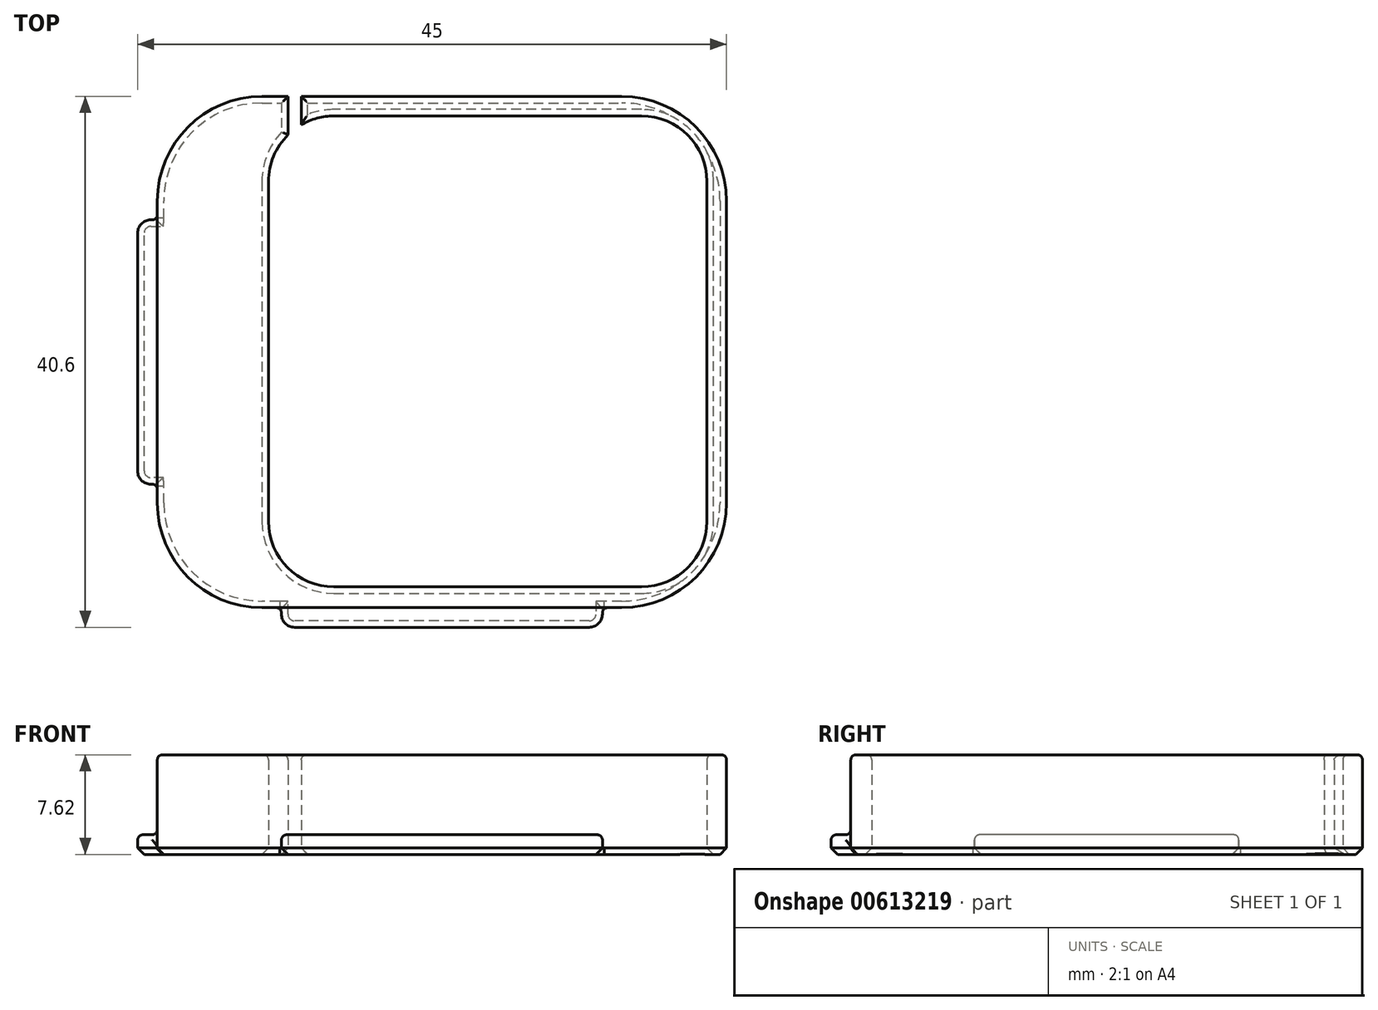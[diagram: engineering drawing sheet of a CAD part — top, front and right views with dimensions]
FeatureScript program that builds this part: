
annotation { "Feature Type Name" : "Feature", "Feature Type Description" : "" }
export const myFeature = defineFeature(function(context is Context, id is Id, definition is map)
    precondition{}
    {
        {
            var Q0;
            Q0=qCreatedBy(makeId("Top.planeOp"),FACE);
            var sketch = newSketch(context, id + "F0", { "sketchPlane" : qUnion([Q0])});
            skLineSegment(sketch, "E0.bottom", {"start": v(-14.69, 21.76) * mm, "end": v(-13.19, 21.76) * mm});
            skLineSegment(sketch, "E0.top", {"start": v(-14.69, -17.34) * mm, "end": v(12.81, -17.34) * mm});
            skLineSegment(sketch, "E0.left", {"start": v(-22.69, 13.76) * mm, "end": v(-22.69, -9.34) * mm});
            skLineSegment(sketch, "E0.right", {"start": v(20.81, 13.76) * mm, "end": v(20.81, -9.34) * mm});
            skLineSegment(sketch, "E1.bottom", {"start": v(14.31, 20.26) * mm, "end": v(-9.19, 20.26) * mm});
            skLineSegment(sketch, "E1.top", {"start": v(14.31, -15.74) * mm, "end": v(-9.19, -15.74) * mm});
            skLineSegment(sketch, "E1.left", {"start": v(19.31, 15.26) * mm, "end": v(19.31, -10.74) * mm});
            skLineSegment(sketch, "E1.right", {"start": v(-14.19, 15.26) * mm, "end": v(-14.19, -10.74) * mm});
            skPoint(sketch, "E2.visualSharp", {"position": v(-14.19, 20.26) * mm});
            skArc(sketch, "E2.filletArc", {"start": v(-9.19, 20.26) * mm, "mid": v(-10.48, 20.09) * mm, "end": v(-11.69, 19.59) * mm});
            skPoint(sketch, "E3.visualSharp", {"position": v(-14.19, -15.74) * mm});
            skArc(sketch, "E3.filletArc", {"start": v(-14.19, -10.74) * mm, "mid": v(-12.72, -14.28) * mm, "end": v(-9.19, -15.74) * mm});
            skPoint(sketch, "E4.visualSharp", {"position": v(19.31, -15.74) * mm});
            skArc(sketch, "E4.filletArc", {"start": v(14.31, -15.74) * mm, "mid": v(17.85, -14.28) * mm, "end": v(19.31, -10.74) * mm});
            skPoint(sketch, "E5.visualSharp", {"position": v(19.31, 20.26) * mm});
            skArc(sketch, "E5.filletArc", {"start": v(19.31, 15.26) * mm, "mid": v(17.85, 18.8) * mm, "end": v(14.31, 20.26) * mm});
            skPoint(sketch, "E6.visualSharp", {"position": v(-22.69, -17.34) * mm});
            skArc(sketch, "E6.filletArc", {"start": v(-22.69, -9.34) * mm, "mid": v(-20.35, -15) * mm, "end": v(-14.69, -17.34) * mm});
            skPoint(sketch, "E7.visualSharp", {"position": v(-22.69, 21.76) * mm});
            skArc(sketch, "E7.filletArc", {"start": v(-14.69, 21.76) * mm, "mid": v(-20.35, 19.41) * mm, "end": v(-22.69, 13.76) * mm});
            skPoint(sketch, "E8.visualSharp", {"position": v(20.81, 21.76) * mm});
            skArc(sketch, "E8.filletArc", {"start": v(20.81, 13.76) * mm, "mid": v(18.47, 19.41) * mm, "end": v(12.81, 21.76) * mm});
            skPoint(sketch, "E9.visualSharp", {"position": v(20.81, -17.34) * mm});
            skArc(sketch, "E9.filletArc", {"start": v(12.81, -17.34) * mm, "mid": v(18.47, -15) * mm, "end": v(20.81, -9.34) * mm});
            skLineSegment(sketch, "E10", {"start": v(-12.69, 21.76) * mm, "end": v(-12.69, 18.83) * mm});
            skLineSegment(sketch, "E11", {"start": v(-11.69, 19.59) * mm, "end": v(-11.69, 21.76) * mm});
            skArc(sketch, "E12", {"start": v(-12.69, 18.83) * mm, "mid": v(-13.8, 17.2) * mm, "end": v(-14.19, 15.26) * mm});
            skLineSegment(sketch, "E13", {"start": v(-11.69, 21.76) * mm, "end": v(12.81, 21.76) * mm});
            skLineSegment(sketch, "E14", {"start": v(-13.19, 21.76) * mm, "end": v(-12.69, 21.76) * mm});
            skSolve(sketch);
        }
        {
            var Q0;
            Q0=qSketchRegion(id+"F0",true);
            extrude(context, id + "F1", {"entities" : qUnion([Q0]), "depth" : 7.62 * mm});
        }
        {
            var Q0;
            Q0=qCreatedBy(makeId("Top.planeOp"),FACE);
            var sketch = newSketch(context, id + "F2", { "sketchPlane" : qUnion([Q0])});
            skLineSegment(sketch, "E15.0", {"start": v(-22.69, 13.76) * mm, "end": v(-22.69, -9.34) * mm});
            skLineSegment(sketch, "E15.1", {"start": v(-14.69, -17.34) * mm, "end": v(12.81, -17.34) * mm});
            skLineSegment(sketch, "E16.bottom", {"start": v(-22.69, 12.31) * mm, "end": v(-23.19, 12.31) * mm});
            skLineSegment(sketch, "E16.top", {"start": v(-22.69, -7.9) * mm, "end": v(-23.19, -7.9) * mm});
            skLineSegment(sketch, "E16.left", {"start": v(-22.69, 12.31) * mm, "end": v(-22.69, -7.9) * mm});
            skLineSegment(sketch, "E16.right", {"start": v(-24.19, 11.31) * mm, "end": v(-24.19, -6.9) * mm});
            skPoint(sketch, "E17", {"position": v(-24.19, 2.2) * mm});
            skPoint(sketch, "E18.visualSharp", {"position": v(-24.19, 12.31) * mm});
            skArc(sketch, "E18.filletArc", {"start": v(-23.19, 12.31) * mm, "mid": v(-23.9, 12.02) * mm, "end": v(-24.19, 11.31) * mm});
            skPoint(sketch, "E19.visualSharp", {"position": v(-24.19, -7.9) * mm});
            skArc(sketch, "E19.filletArc", {"start": v(-24.19, -6.9) * mm, "mid": v(-23.9, -7.6) * mm, "end": v(-23.19, -7.9) * mm});
            skPoint(sketch, "E20", {"position": v(-22.69, 2.2) * mm});
            skLineSegment(sketch, "E21.bottom", {"start": v(-13.2, -17.34) * mm, "end": v(11.33, -17.34) * mm});
            skLineSegment(sketch, "E21.top", {"start": v(-12.2, -18.84) * mm, "end": v(10.33, -18.84) * mm});
            skLineSegment(sketch, "E21.left", {"start": v(-13.2, -17.34) * mm, "end": v(-13.2, -17.84) * mm});
            skLineSegment(sketch, "E21.right", {"start": v(11.33, -17.34) * mm, "end": v(11.33, -17.84) * mm});
            skPoint(sketch, "E22", {"position": v(-0.94, -17.34) * mm});
            skPoint(sketch, "E23", {"position": v(-0.94, -18.84) * mm});
            skPoint(sketch, "E24.visualSharp", {"position": v(-13.2, -18.84) * mm});
            skArc(sketch, "E24.filletArc", {"start": v(-13.2, -17.84) * mm, "mid": v(-12.91, -18.55) * mm, "end": v(-12.2, -18.84) * mm});
            skPoint(sketch, "E25.visualSharp", {"position": v(11.33, -18.84) * mm});
            skArc(sketch, "E25.filletArc", {"start": v(10.33, -18.84) * mm, "mid": v(11.03, -18.55) * mm, "end": v(11.33, -17.84) * mm});
            skSolve(sketch);
        }
        {
            var Q0;
            Q0=qSketchRegion(id+"F2",true);
            extrude(context, id + "F3", {"entities" : qUnion([Q0]), "operationType" : NewBodyOperationType.ADD, "depth" : 1.5 * mm});
        }
        {
            var Q0;
            Q0=makeQuery(id+"F1.opExtrude","CAP_FACE",FACE,{"disambiguationData":[OSD([sQuery(id+"F0.wireOp",EDGE,"E0.bottom"),sQuery(id+"F0.wireOp",EDGE,"E0.top"),sQuery(id+"F0.wireOp",EDGE,"E0.left"),sQuery(id+"F0.wireOp",EDGE,"E0.right"),sQuery(id+"F0.wireOp",EDGE,"E1.bottom"),sQuery(id+"F0.wireOp",EDGE,"E1.top"),sQuery(id+"F0.wireOp",EDGE,"E1.left"),sQuery(id+"F0.wireOp",EDGE,"E1.right"),sQuery(id+"F0.wireOp",EDGE,"E2.filletArc"),sQuery(id+"F0.wireOp",EDGE,"E3.filletArc"),sQuery(id+"F0.wireOp",EDGE,"E4.filletArc"),sQuery(id+"F0.wireOp",EDGE,"E5.filletArc"),sQuery(id+"F0.wireOp",EDGE,"E6.filletArc"),sQuery(id+"F0.wireOp",EDGE,"E7.filletArc"),sQuery(id+"F0.wireOp",EDGE,"E8.filletArc"),sQuery(id+"F0.wireOp",EDGE,"E9.filletArc"),sQuery(id+"F0.wireOp",EDGE,"E10"),sQuery(id+"F0.wireOp",EDGE,"E11"),sQuery(id+"F0.wireOp",EDGE,"E12"),sQuery(id+"F0.wireOp",EDGE,"E13")])],"isStart":false});
            var Q1;
            Q1=makeQuery(id+"F3.opExtrude","CAP_FACE",FACE,{"disambiguationData":[OSD([sQuery(id+"F2.wireOp",EDGE,"E21.bottom"),sQuery(id+"F2.wireOp",EDGE,"E21.top"),sQuery(id+"F2.wireOp",EDGE,"E21.left"),sQuery(id+"F2.wireOp",EDGE,"E21.right"),sQuery(id+"F2.wireOp",EDGE,"E24.filletArc"),sQuery(id+"F2.wireOp",EDGE,"E25.filletArc")])],"isStart":false});
            var Q2;
            Q2=makeQuery(id+"F3.opExtrude","CAP_FACE",FACE,{"disambiguationData":[OSD([sQuery(id+"F2.wireOp",EDGE,"E16.bottom"),sQuery(id+"F2.wireOp",EDGE,"E16.top"),sQuery(id+"F2.wireOp",EDGE,"E16.left"),sQuery(id+"F2.wireOp",EDGE,"E16.right"),sQuery(id+"F2.wireOp",EDGE,"E18.filletArc"),sQuery(id+"F2.wireOp",EDGE,"E19.filletArc")])],"isStart":false});
            fillet(context, id + "F4", {"entities" : qUnion([Q0, Q1, Q2]), "radius" : 0.4 * mm, "tangentPropagation" : true, "allowEdgeOverflow" : false});
        }
        {
            var Q0;
            Q0=makeQuery(id+"F3.boolean.opBoolean","MERGE",FACE,{"derivedFrom":[makeQuery(id+"F1.opExtrude","CAP_FACE",FACE,{"disambiguationData":[OSD([sQuery(id+"F0.wireOp",EDGE,"E0.bottom"),sQuery(id+"F0.wireOp",EDGE,"E0.top"),sQuery(id+"F0.wireOp",EDGE,"E0.left"),sQuery(id+"F0.wireOp",EDGE,"E0.right"),sQuery(id+"F0.wireOp",EDGE,"E1.bottom"),sQuery(id+"F0.wireOp",EDGE,"E1.top"),sQuery(id+"F0.wireOp",EDGE,"E1.left"),sQuery(id+"F0.wireOp",EDGE,"E1.right"),sQuery(id+"F0.wireOp",EDGE,"E2.filletArc"),sQuery(id+"F0.wireOp",EDGE,"E3.filletArc"),sQuery(id+"F0.wireOp",EDGE,"E4.filletArc"),sQuery(id+"F0.wireOp",EDGE,"E5.filletArc"),sQuery(id+"F0.wireOp",EDGE,"E6.filletArc"),sQuery(id+"F0.wireOp",EDGE,"E7.filletArc"),sQuery(id+"F0.wireOp",EDGE,"E8.filletArc"),sQuery(id+"F0.wireOp",EDGE,"E9.filletArc"),sQuery(id+"F0.wireOp",EDGE,"E10"),sQuery(id+"F0.wireOp",EDGE,"E11"),sQuery(id+"F0.wireOp",EDGE,"E12"),sQuery(id+"F0.wireOp",EDGE,"E13"),sQuery(id+"F0.wireOp",EDGE,"E14")])],"isStart":true}),makeQuery(id+"F3.opExtrude","CAP_FACE",FACE,{"disambiguationData":[OSD([sQuery(id+"F2.wireOp",EDGE,"E16.bottom"),sQuery(id+"F2.wireOp",EDGE,"E16.top"),sQuery(id+"F2.wireOp",EDGE,"E16.left"),sQuery(id+"F2.wireOp",EDGE,"E16.right"),sQuery(id+"F2.wireOp",EDGE,"E18.filletArc"),sQuery(id+"F2.wireOp",EDGE,"E19.filletArc")])],"isStart":true}),makeQuery(id+"F3.opExtrude","CAP_FACE",FACE,{"disambiguationData":[OSD([sQuery(id+"F2.wireOp",EDGE,"E21.bottom"),sQuery(id+"F2.wireOp",EDGE,"E21.top"),sQuery(id+"F2.wireOp",EDGE,"E21.left"),sQuery(id+"F2.wireOp",EDGE,"E21.right"),sQuery(id+"F2.wireOp",EDGE,"E24.filletArc"),sQuery(id+"F2.wireOp",EDGE,"E25.filletArc")])],"isStart":true})]});
            chamfer(context, id + "F5", {"entities" : qUnion([Q0]), "width" : .5 * mm, "tangentPropagation" : true});
        }
    });
